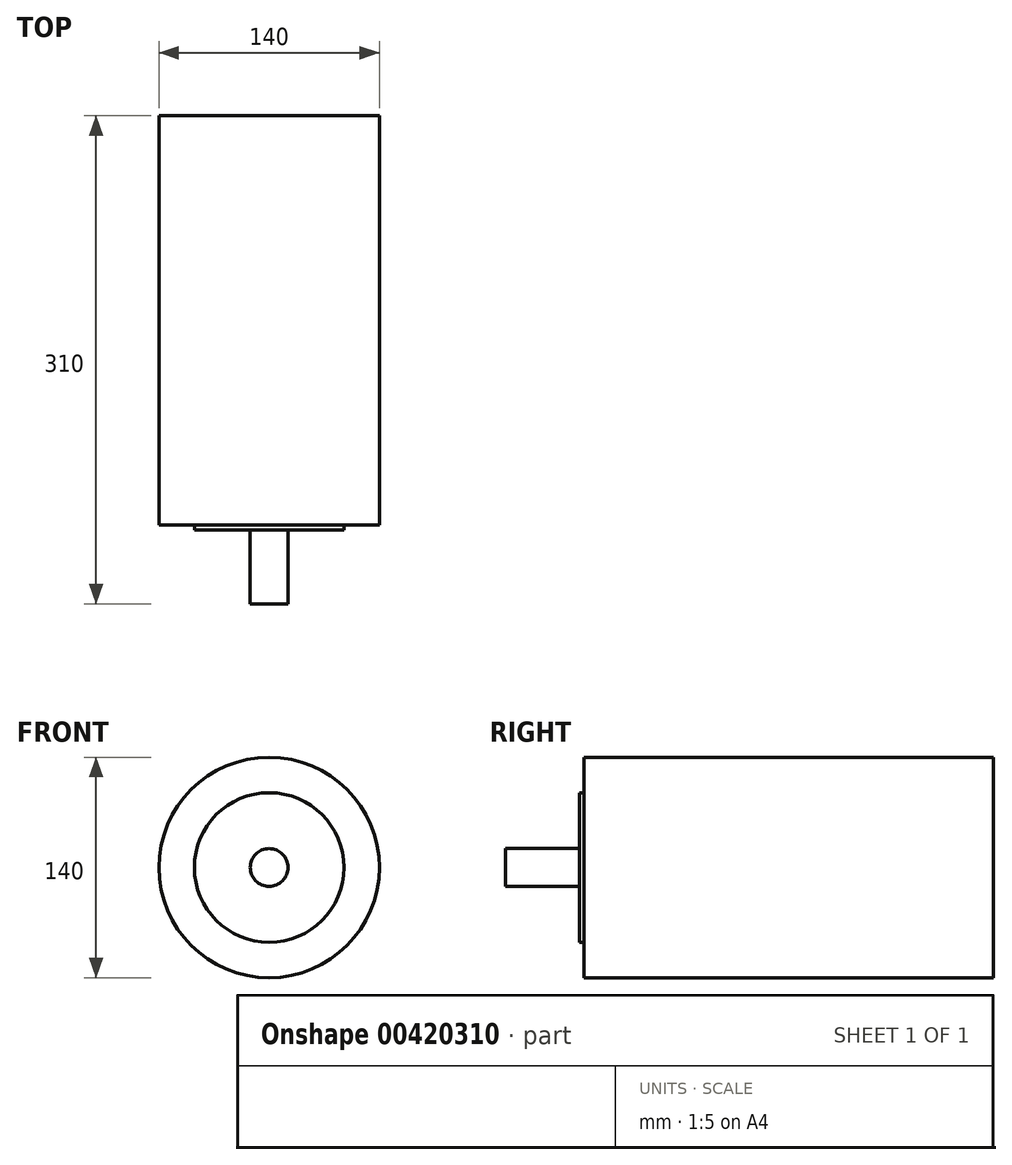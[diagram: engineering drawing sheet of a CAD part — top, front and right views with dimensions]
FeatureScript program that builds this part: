
annotation { "Feature Type Name" : "Feature", "Feature Type Description" : "" }
export const myFeature = defineFeature(function(context is Context, id is Id, definition is map)
    precondition{}
    {
        {
            var Q0;
            Q0=qCreatedBy(makeId("Front.planeOp"),FACE);
            var sketch = newSketch(context, id + "F0", { "sketchPlane" : qUnion([Q0])});
            skCircle(sketch, "E0", {"center": v(0, 0) * mm, "radius": 12 * mm});
            skCircle(sketch, "E1", {"center": v(0, 0) * mm, "radius": 47.5 * mm});
            skCircle(sketch, "E2", {"center": v(0, 0) * mm, "radius": 70 * mm});
            skSolve(sketch);
        }
        {
            var Q0;
            Q0=makeQuery(id+"F0.imprint","IMPRINT",FACE,{"disambiguationData":[TD([[makeQuery(id+"F0.imprint","IMPRINT",EDGE,{"derivedFrom":sQuery(id+"F0.wireOp",EDGE,"E0")}),1.0]])]});
            extrude(context, id + "F1", {"entities" : qUnion([Q0]), "depth" : 50 * mm});
        }
        {
            var Q0;
            Q0=makeQuery(id+"F0.imprint","IMPRINT",FACE,{"disambiguationData":[TD([[makeQuery(id+"F0.imprint","IMPRINT",EDGE,{"derivedFrom":sQuery(id+"F0.wireOp",EDGE,"E0")}),-1.0]])]});
            extrude(context, id + "F2", {"entities" : qUnion([Q0]), "operationType" : NewBodyOperationType.ADD, "depth" : 3 * mm});
        }
        {
            var Q0;
            Q0=makeQuery(id+"F0.imprint","IMPRINT",FACE,{"disambiguationData":[TD([[makeQuery(id+"F0.imprint","IMPRINT",EDGE,{"derivedFrom":sQuery(id+"F0.wireOp",EDGE,"E1")}),-1.0]])]});
            var Q1;
            Q1=makeQuery(id+"F0.imprint","IMPRINT",FACE,{"disambiguationData":[TD([[makeQuery(id+"F0.imprint","IMPRINT",EDGE,{"derivedFrom":sQuery(id+"F0.wireOp",EDGE,"E0")}),-1.0]])]});
            var Q2;
            Q2=makeQuery(id+"F0.imprint","IMPRINT",FACE,{"disambiguationData":[TD([[makeQuery(id+"F0.imprint","IMPRINT",EDGE,{"derivedFrom":sQuery(id+"F0.wireOp",EDGE,"E0")}),1.0]])]});
            extrude(context, id + "F3", {"entities" : qUnion([Q0, Q1, Q2]), "operationType" : NewBodyOperationType.ADD, "oppositeDirection" : true, "depth" : 260 * mm});
        }
    });
